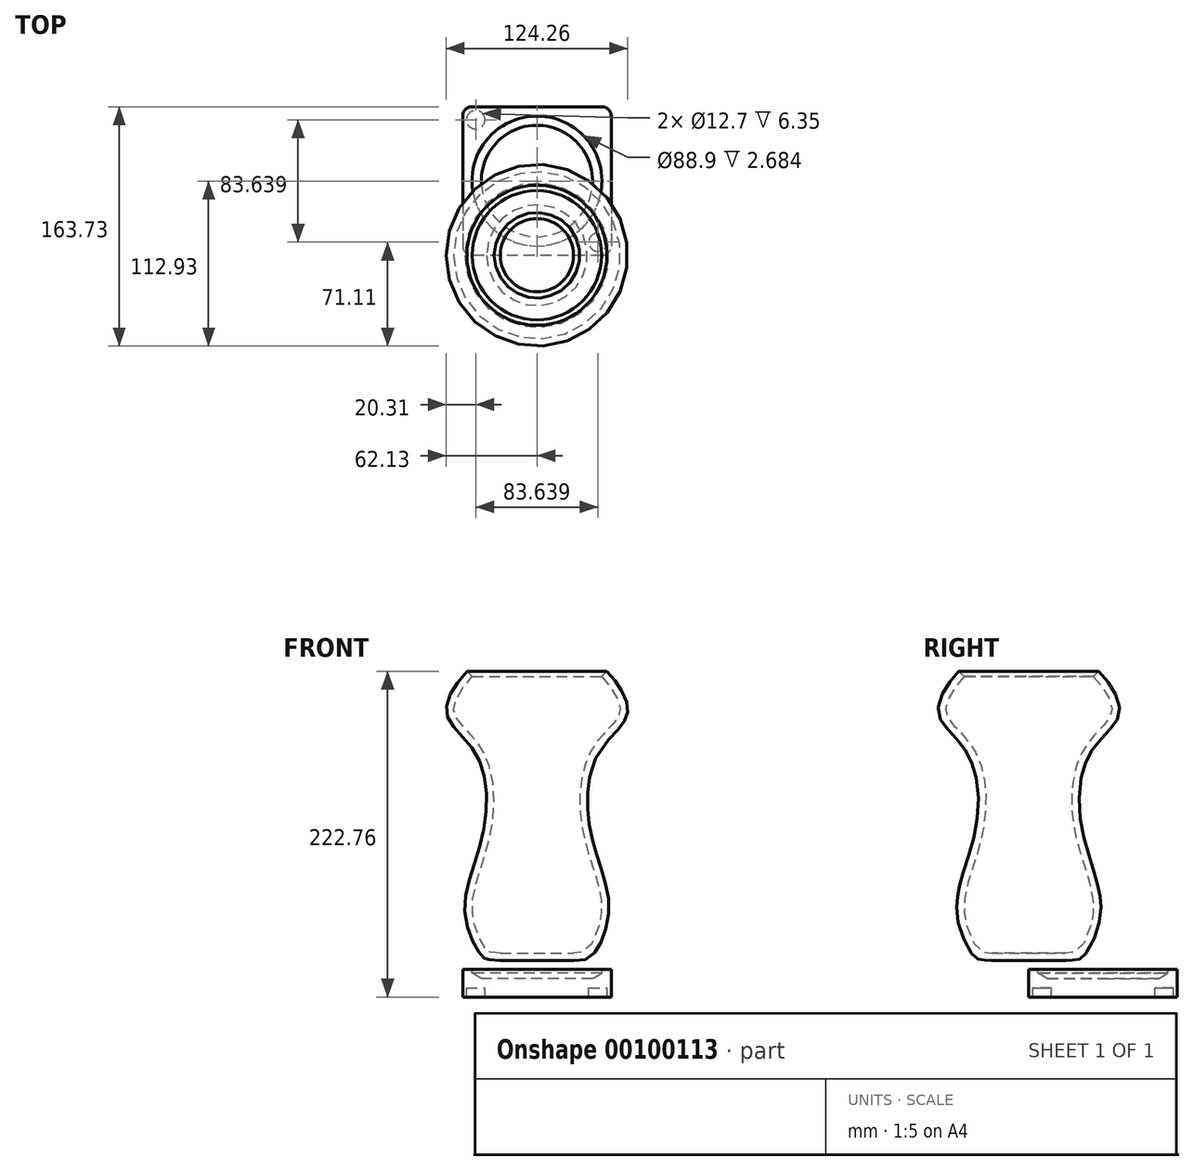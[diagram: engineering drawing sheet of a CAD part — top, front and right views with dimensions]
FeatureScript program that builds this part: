
annotation { "Feature Type Name" : "Feature", "Feature Type Description" : "" }
export const myFeature = defineFeature(function(context is Context, id is Id, definition is map)
    precondition{}
    {
        {
            var Q0;
            Q0=qCreatedBy(makeId("Top.planeOp"),FACE);
            var sketch = newSketch(context, id + "F0", { "sketchPlane" : qUnion([Q0])});
            skLineSegment(sketch, "E0.bottom", {"start": v(50.8, 50.8) * mm, "end": v(-50.8, 50.8) * mm});
            skLineSegment(sketch, "E0.top", {"start": v(50.8, -50.8) * mm, "end": v(-50.8, -50.8) * mm});
            skLineSegment(sketch, "E0.left", {"start": v(50.8, 50.8) * mm, "end": v(50.8, -50.8) * mm});
            skLineSegment(sketch, "E0.right", {"start": v(-50.8, 50.8) * mm, "end": v(-50.8, -50.8) * mm});
            skPoint(sketch, "E0.middle", {"position": v(0, 0) * mm});
            skSolve(sketch);
        }
        {
            var Q0;
            Q0=makeQuery(id+"F0.imprint","IMPRINT",FACE,{"disambiguationData":[TD([[makeQuery(id+"F0.imprint","IMPRINT",EDGE,{"derivedFrom":sQuery(id+"F0.wireOp",EDGE,"E0.bottom")}),1.0]])]});
            extrude(context, id + "F1", {"entities" : qUnion([Q0]), "depth" : 12.7 * mm});
        }
        {
            var Q0;
            Q0=makeQuery(id+"F1.opExtrude","CAP_FACE",FACE,{"disambiguationData":[OSD([sQuery(id+"F0.wireOp",EDGE,"E0.bottom"),sQuery(id+"F0.wireOp",EDGE,"E0.top"),sQuery(id+"F0.wireOp",EDGE,"E0.left"),sQuery(id+"F0.wireOp",EDGE,"E0.right")])],"isStart":false});
            var sketch = newSketch(context, id + "F2", { "sketchPlane" : qUnion([Q0])});
            skCircle(sketch, "E1", {"center": v(0, 0) * mm, "radius": 44.45 * mm});
            skSolve(sketch);
        }
        {
            var Q0;
            Q0=makeQuery(id+"F2.imprint","IMPRINT",FACE,{"disambiguationData":[TD([[makeQuery(id+"F2.imprint","IMPRINT",EDGE,{"derivedFrom":sQuery(id+"F2.wireOp",EDGE,"E1")}),1.0]])]});
            extrude(context, id + "F3", {"entities" : qUnion([Q0]), "operationType" : NewBodyOperationType.REMOVE, "oppositeDirection" : true, "depth" : 6.35 * mm});
        }
        {
            var Q0;
            Q0=makeQuery(id+"F1.opExtrude","CAP_FACE",FACE,{"disambiguationData":[OSD([sQuery(id+"F0.wireOp",EDGE,"E0.bottom"),sQuery(id+"F0.wireOp",EDGE,"E0.top"),sQuery(id+"F0.wireOp",EDGE,"E0.left"),sQuery(id+"F0.wireOp",EDGE,"E0.right")])],"isStart":true});
            var sketch = newSketch(context, id + "F4", { "sketchPlane" : qUnion([Q0])});
            skLineSegment(sketch, "E2", {"start": v(-50.8, 50.8) * mm, "end": v(50.8, -50.8) * mm, "construction": true});
            skLineSegment(sketch, "E3", {"start": v(-50.8, -50.8) * mm, "end": v(50.8, 50.8) * mm, "construction": true});
            skCircle(sketch, "E4", {"center": v(-41.82, 41.82) * mm, "radius": 6.35 * mm});
            skCircle(sketch, "E5.MirrorC", {"center": v(41.82, 41.82) * mm, "radius": 6.35 * mm});
            skLineSegment(sketch, "E6", {"start": v(-50.8, 0) * mm, "end": v(50.8, 0) * mm, "construction": true});
            skCircle(sketch, "E7.MirrorC", {"center": v(41.82, -41.82) * mm, "radius": 6.35 * mm});
            skCircle(sketch, "E8.MirrorC", {"center": v(-41.82, -41.82) * mm, "radius": 6.35 * mm});
            skSolve(sketch);
        }
        {
            var Q0;
            Q0=makeQuery(id+"F4.imprint","IMPRINT",FACE,{"disambiguationData":[TD([[makeQuery(id+"F4.imprint","IMPRINT",EDGE,{"derivedFrom":sQuery(id+"F4.wireOp",EDGE,"E5.MirrorC")}),-1.0]])]});
            var Q1;
            Q1=makeQuery(id+"F4.imprint","IMPRINT",FACE,{"disambiguationData":[TD([[makeQuery(id+"F4.imprint","IMPRINT",EDGE,{"derivedFrom":sQuery(id+"F4.wireOp",EDGE,"E7.MirrorC")}),1.0]])]});
            var Q2;
            Q2=makeQuery(id+"F4.imprint","IMPRINT",FACE,{"disambiguationData":[TD([[makeQuery(id+"F4.imprint","IMPRINT",EDGE,{"derivedFrom":sQuery(id+"F4.wireOp",EDGE,"E8.MirrorC")}),-1.0]])]});
            var Q3;
            Q3=makeQuery(id+"F4.imprint","IMPRINT",FACE,{"disambiguationData":[TD([[makeQuery(id+"F4.imprint","IMPRINT",EDGE,{"derivedFrom":sQuery(id+"F4.wireOp",EDGE,"E4")}),1.0]])]});
            extrude(context, id + "F5", {"entities" : qUnion([Q0, Q1, Q2, Q3]), "operationType" : NewBodyOperationType.ADD, "depth" : 6.35 * mm});
        }
        {
            var Q0;
            Q0=makeQuery(id+"F1.opExtrude","SWEPT_EDGE",EDGE,{"disambiguationData":[OSD([sQuery(id+"F0.wireOp",EDGE,"E0.top"),sQuery(id+"F0.wireOp",EDGE,"E0.right")])]});
            var Q1;
            Q1=makeQuery(id+"F1.opExtrude","SWEPT_EDGE",EDGE,{"disambiguationData":[OSD([sQuery(id+"F0.wireOp",EDGE,"E0.top"),sQuery(id+"F0.wireOp",EDGE,"E0.left")])]});
            var Q2;
            Q2=makeQuery(id+"F1.opExtrude","SWEPT_EDGE",EDGE,{"disambiguationData":[OSD([sQuery(id+"F0.wireOp",EDGE,"E0.bottom"),sQuery(id+"F0.wireOp",EDGE,"E0.right")])]});
            var Q3;
            Q3=makeQuery(id+"F1.opExtrude","SWEPT_EDGE",EDGE,{"disambiguationData":[OSD([sQuery(id+"F0.wireOp",EDGE,"E0.bottom"),sQuery(id+"F0.wireOp",EDGE,"E0.left")])]});
            fillet(context, id + "F6", {"entities" : qUnion([Q0, Q1, Q2, Q3]), "radius" : 6.35 * mm, "tangentPropagation" : true, "allowEdgeOverflow" : false});
        }
        {
            var Q0;
            Q0=makeQuery(id+"F3.boolean.opBoolean","COPY",FACE,{"derivedFrom":makeQuery(id+"F3.opExtrude","CAP_FACE",FACE,{"disambiguationData":[OSD([sQuery(id+"F2.wireOp",EDGE,"E1")])],"isStart":false})});
            chamfer(context, id + "F7", {"entities" : qUnion([Q0]), "chamferType" : ChamferType.OFFSET_ANGLE, "width" : 6.35 * mm, "oppositeDirection" : false, "angle" : 30 * degree, "tangentPropagation" : true});
        }
        {
            var Q0;
            Q0=makeQuery(id+"F1.opExtrude","SWEPT_FACE",FACE,{"disambiguationData":[OSD([sQuery(id+"F0.wireOp",EDGE,"E0.top")])]});
            var sketch = newSketch(context, id + "F8", { "sketchPlane" : qUnion([Q0])});
            skLineSegment(sketch, "E9", {"start": v(0, 18.6) * mm, "end": v(25.4, 18.6) * mm});
            skLineSegment(sketch, "E10", {"start": v(0, 0) * mm, "end": v(0, 51.24) * mm, "construction": true});
            skPoint(sketch, "E10.endSnap0", {"position": v(0, 12.7) * mm});
            skFitSpline(sketch, "E11", {"points": [v(25.4, 18.6) * mm, v(37, 20.97) * mm, v(49.22, 51.61) * mm, v(37, 105.5) * mm, v(42.16, 160.7) * mm, v(61.91, 187.67) * mm, v(47.93, 216.4) * mm], "startDerivative": vector(226.12, 29.95) * mm, "endDerivative": vector(-148.74, 161.53) * mm});
            skFitSpline(sketch, "E12.0", {"points": [v(24.73, 23.67) * mm, v(26, 23.84) * mm, v(28.23, 24.07) * mm, v(30.76, 24.22) * mm, v(32.18, 24.3) * mm, v(32.85, 24.4) * mm, v(33.12, 24.45) * mm, v(33.2, 24.48) * mm, v(33.2, 24.48) * mm, v(33.25, 24.5) * mm, v(33.42, 24.62) * mm, v(33.75, 24.92) * mm, v(34.36, 25.56) * mm, v(35.3, 26.74) * mm, v(36.58, 28.66) * mm, v(37.92, 31) * mm, v(39.26, 33.68) * mm, v(40.96, 37.63) * mm, v(42.42, 42) * mm, v(43.46, 46.57) * mm, v(43.9, 49.46) * mm, v(44.12, 51.74) * mm, v(44.22, 54.02) * mm, v(44.18, 56.9) * mm, v(43.86, 60.42) * mm, v(43.13, 65.22) * mm, v(41.68, 71.4) * mm, v(39.36, 79.14) * mm, v(37.18, 85.88) * mm, v(35.44, 91.45) * mm, v(34.17, 95.72) * mm, v(33.19, 99.37) * mm, v(32.46, 102.34) * mm, v(31.78, 105.35) * mm, v(31.04, 109.16) * mm, v(30.33, 113.78) * mm, v(29.81, 118.43) * mm, v(29.38, 124.64) * mm, v(29.34, 132.38) * mm, v(30.04, 139.93) * mm, v(31.09, 145.79) * mm, v(32.12, 150.07) * mm, v(33.43, 154.2) * mm, v(35.02, 158.18) * mm, v(36.44, 161.03) * mm, v(37.48, 162.86) * mm, v(38.2, 164.06) * mm, v(39.15, 165.51) * mm, v(40.32, 167.17) * mm, v(41.93, 169.28) * mm, v(44, 171.74) * mm, v(46.48, 174.46) * mm, v(48.86, 177) * mm, v(51.07, 179.36) * mm, v(53.01, 181.57) * mm, v(54.62, 183.65) * mm, v(55.62, 185.24) * mm, v(56.2, 186.43) * mm, v(56.55, 187.28) * mm, v(56.75, 187.96) * mm, v(56.87, 188.5) * mm, v(56.96, 189.02) * mm, v(57.02, 189.73) * mm, v(57.02, 190.95) * mm, v(56.8, 192.64) * mm, v(56.18, 194.93) * mm, v(55.2, 197.39) * mm, v(53.9, 199.97) * mm, v(51.8, 203.5) * mm, v(48.56, 207.96) * mm, v(45.64, 211.34) * mm, v(44.17, 212.94) * mm]});
            skLineSegment(sketch, "E12.1", {"start": v(0, 23.72) * mm, "end": v(25.07, 23.72) * mm});
            skLineSegment(sketch, "E13", {"start": v(0, 18.6) * mm, "end": v(0, 23.72) * mm});
            skLineSegment(sketch, "E14", {"start": v(44.17, 212.94) * mm, "end": v(47.93, 216.4) * mm});
            skSolve(sketch);
        }
        {
            var Q0;
            Q0=makeQuery(id+"F8.imprint","IMPRINT",FACE,{"disambiguationData":[TD([[makeQuery(id+"F8.imprint","IMPRINT",EDGE,{"derivedFrom":sQuery(id+"F8.wireOp",EDGE,"E9")}),1.0]])]});
            var Q1;
            Q1=sQuery(id+"F8.wireOp",EDGE,"E10");
            revolve(context, id + "F9", {"entities" : qUnion([Q0]), "axis" : qUnion([Q1]), "revolveType" : RevolveType.FULL});
        }
    });
